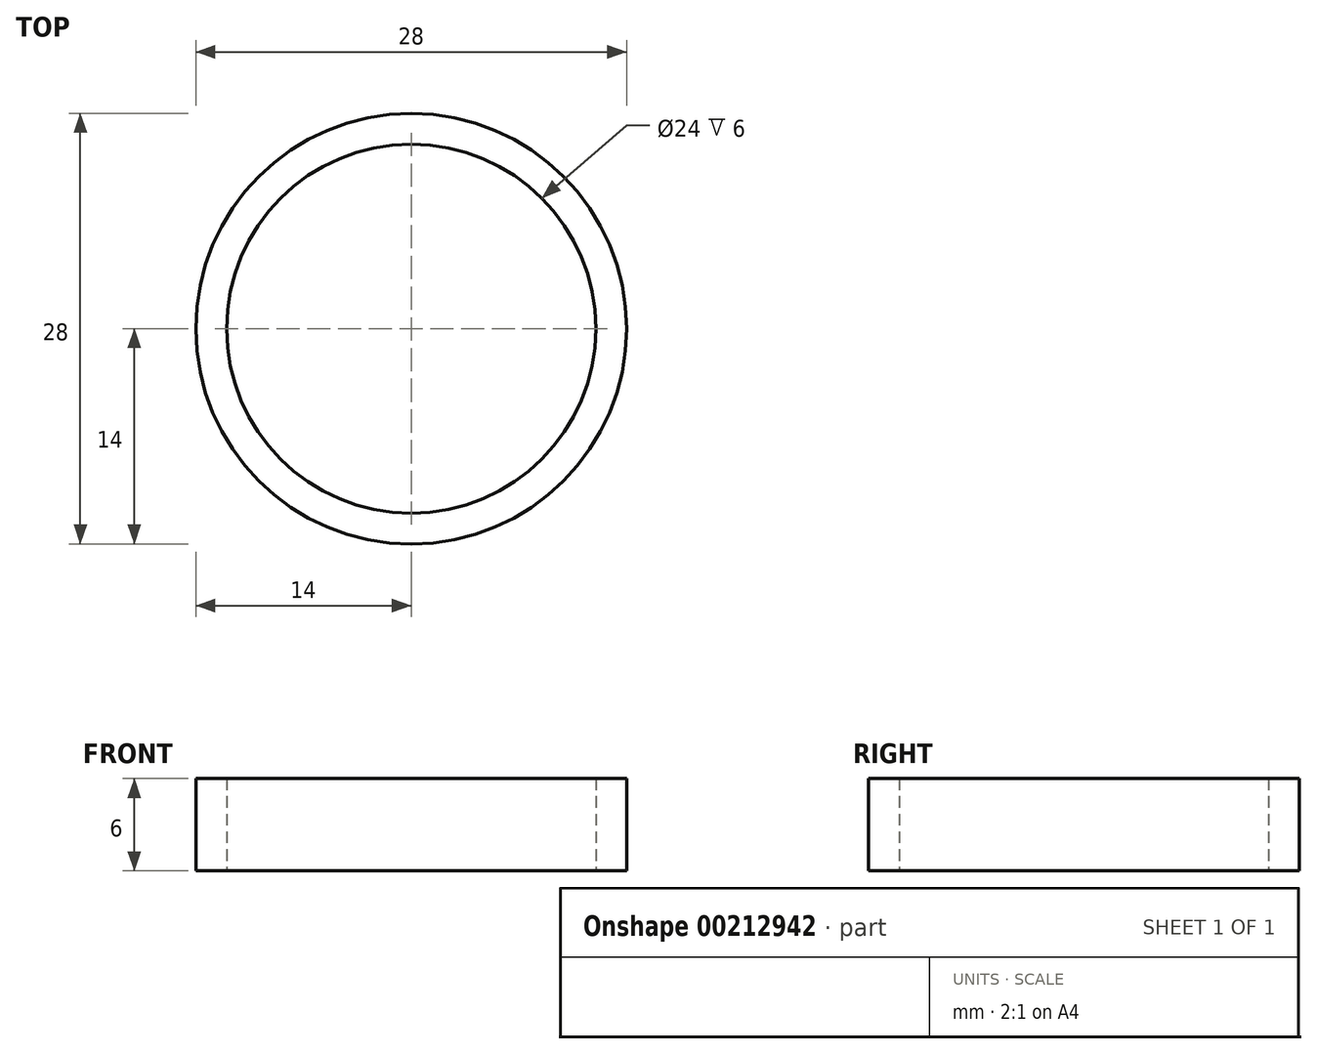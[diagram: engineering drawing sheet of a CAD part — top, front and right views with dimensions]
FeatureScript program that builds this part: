
annotation { "Feature Type Name" : "Feature", "Feature Type Description" : "" }
export const myFeature = defineFeature(function(context is Context, id is Id, definition is map)
    precondition{}
    {
        {
            var Q0;
            Q0=qCreatedBy(makeId("Top.planeOp"),FACE);
            var sketch = newSketch(context, id + "F0", { "sketchPlane" : qUnion([Q0])});
            skCircle(sketch, "E0", {"center": v(0, 0) * mm, "radius": 14 * mm});
            skCircle(sketch, "E1", {"center": v(0, 0) * mm, "radius": 12 * mm});
            skSolve(sketch);
        }
        {
            var Q0;
            Q0 = qSketchRegion(id + "F0", true);
            extrude(context, id + "F1", {"entities" : qUnion([Q0]), "depth" : 6 * mm});
        }
    });
